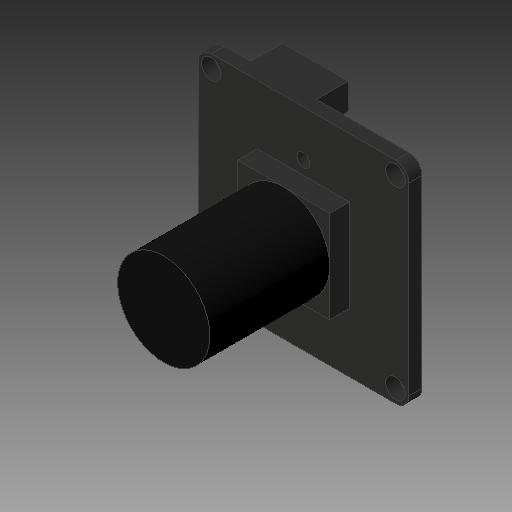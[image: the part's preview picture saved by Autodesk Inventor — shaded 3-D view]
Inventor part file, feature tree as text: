
AUTODESK INVENTOR PART (.ipt)
format: ipt  version: 2019 (Build 230136000, 136)  size: 195,072 bytes
history: native  units: mm
features: extrude x6, sketch x6, other x1, fillet x1
ambient origin geometry x8: Origin, YZ Plane, XZ Plane, XY Plane, X Axis, Y Axis, Z Axis, Center Point
bodies: Body1 (feature_tree)
feature tree (14):
  other  "솔리드1"
  extrude  "돌출1"  Depth=32.0mm
  extrude  "돌출2"  Depth=32.0mm
  extrude  "돌출3"  Depth=16.0mm
  extrude  "돌출4"  Depth=16.0mm
  extrude  "돌출5"  Depth=2.0mm TaperAngle=0.0deg
  extrude  "돌출6"  Depth=3.0mm
  fillet  "모깎기1"  Radius=3.0mm
  sketch  "스케치1"
  sketch  "스케치2"
  sketch  "스케치3"
  sketch  "스케치4"
  sketch  "스케치5"
  sketch  "스케치6"
